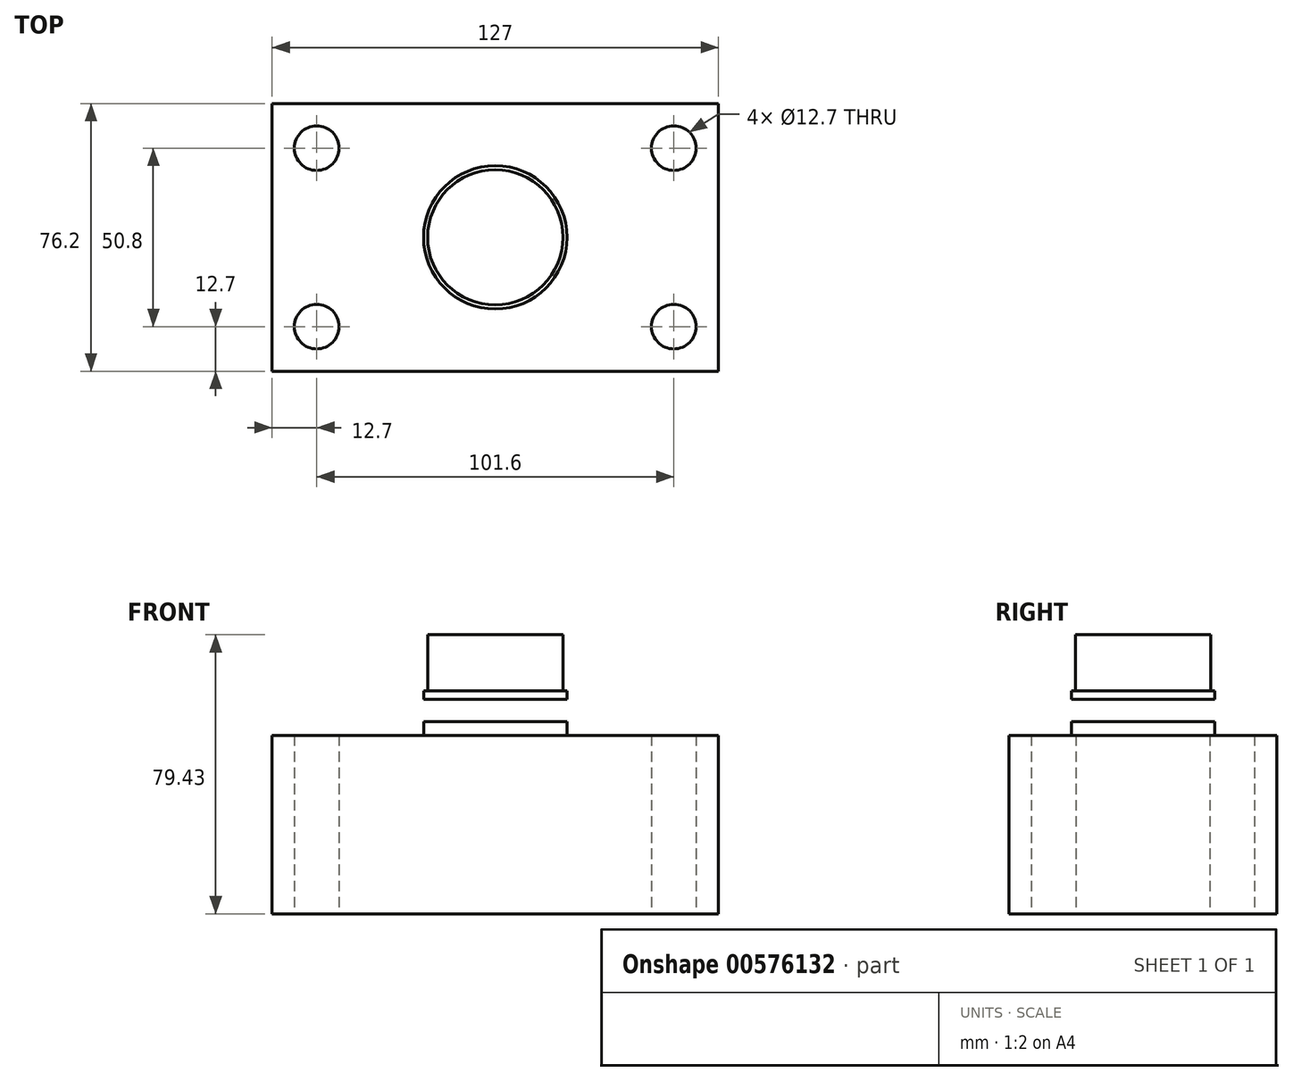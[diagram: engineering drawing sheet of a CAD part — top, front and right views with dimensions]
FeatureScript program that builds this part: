
annotation { "Feature Type Name" : "Feature", "Feature Type Description" : "" }
export const myFeature = defineFeature(function(context is Context, id is Id, definition is map)
    precondition{}
    {
        {
            var Q0;
            Q0=qCreatedBy(makeId("Top.planeOp"),FACE);
            var sketch = newSketch(context, id + "F0", { "sketchPlane" : qUnion([Q0])});
            skLineSegment(sketch, "E0.bottom", {"start": v(-63.5, 38.1) * mm, "end": v(63.5, 38.1) * mm});
            skLineSegment(sketch, "E0.top", {"start": v(-63.5, -38.1) * mm, "end": v(63.5, -38.1) * mm});
            skLineSegment(sketch, "E0.left", {"start": v(-63.5, 38.1) * mm, "end": v(-63.5, -38.1) * mm});
            skLineSegment(sketch, "E0.right", {"start": v(63.5, 38.1) * mm, "end": v(63.5, -38.1) * mm});
            skPoint(sketch, "E0.middle", {"position": v(0, 0) * mm});
            skCircle(sketch, "E1", {"center": v(-50.8, 25.4) * mm, "radius": 6.35 * mm});
            skCircle(sketch, "E2", {"center": v(-50.8, -25.4) * mm, "radius": 6.35 * mm});
            skCircle(sketch, "E3", {"center": v(50.8, 25.4) * mm, "radius": 6.35 * mm});
            skCircle(sketch, "E4", {"center": v(50.8, -25.4) * mm, "radius": 6.35 * mm});
            skSolve(sketch);
        }
        {
            var Q0;
            Q0 = qSketchRegion(id + "F0", true);
            extrude(context, id + "F1", {"entities" : qUnion([Q0]), "depth" : 50.8 * mm, "offsetDistance" : 25.4 * mm});
        }
        {
            var Q0;
            Q0=qCreatedBy(makeId("Front.planeOp"),FACE);
            var sketch = newSketch(context, id + "F2", { "sketchPlane" : qUnion([Q0])});
            skLineSegment(sketch, "E5.bottom", {"start": v(0, 50.8) * mm, "end": v(20.4, 50.8) * mm});
            skLineSegment(sketch, "E5.top", {"start": v(0, 63.5) * mm, "end": v(20.4, 63.5) * mm});
            skLineSegment(sketch, "E5.left", {"start": v(0, 50.8) * mm, "end": v(0, 63.5) * mm});
            skLineSegment(sketch, "E5.right", {"start": v(20.4, 50.8) * mm, "end": v(20.4, 63.5) * mm});
            skSolve(sketch);
        }
        {
            var Q0;
            Q0=makeQuery(id+"F2.imprint","IMPRINT",FACE,{"disambiguationData":[TD([[makeQuery(id+"F2.imprint","IMPRINT",EDGE,{"derivedFrom":sQuery(id+"F2.wireOp",EDGE,"E5.bottom")}),1.0]])]});
            var Q1;
            Q1=sQuery(id+"F2.wireOp",EDGE,"E5.left");
            revolve(context, id + "F3", {"operationType" : NewBodyOperationType.ADD, "entities" : qUnion([Q0]), "axis" : qUnion([Q1]), "revolveType" : RevolveType.FULL});
        }
        {
            var Q0;
            Q0=qCreatedBy(makeId("Front.planeOp"),FACE);
            var sketch = newSketch(context, id + "F4", { "sketchPlane" : qUnion([Q0])});
            skLineSegment(sketch, "E6.bottom", {"start": v(0, 63.5) * mm, "end": v(19.24, 63.5) * mm});
            skLineSegment(sketch, "E6.top", {"start": v(0, 79.43) * mm, "end": v(19.24, 79.43) * mm});
            skLineSegment(sketch, "E6.left", {"start": v(0, 63.5) * mm, "end": v(0, 79.43) * mm});
            skLineSegment(sketch, "E6.right", {"start": v(19.24, 63.5) * mm, "end": v(19.24, 79.43) * mm});
            skSolve(sketch);
        }
        {
            var Q0;
            Q0=makeQuery(id+"F4.imprint","IMPRINT",FACE,{"disambiguationData":[TD([[makeQuery(id+"F4.imprint","IMPRINT",EDGE,{"derivedFrom":sQuery(id+"F4.wireOp",EDGE,"E6.bottom")}),1.0]])]});
            var Q1;
            Q1=sQuery(id+"F4.wireOp",EDGE,"E6.left");
            revolve(context, id + "F5", {"operationType" : NewBodyOperationType.ADD, "entities" : qUnion([Q0]), "axis" : qUnion([Q1]), "revolveType" : RevolveType.FULL});
        }
        {
            var Q0;
            Q0=qCreatedBy(makeId("Front.planeOp"),FACE);
            var sketch = newSketch(context, id + "F6", { "sketchPlane" : qUnion([Q0])});
            skLineSegment(sketch, "E7.bottom", {"start": v(0, 54.68) * mm, "end": v(38.1, 54.68) * mm});
            skLineSegment(sketch, "E7.top", {"start": v(0, 61.03) * mm, "end": v(38.1, 61.03) * mm});
            skLineSegment(sketch, "E7.left", {"start": v(0, 54.68) * mm, "end": v(0, 61.03) * mm});
            skLineSegment(sketch, "E7.right", {"start": v(38.1, 54.68) * mm, "end": v(38.1, 61.03) * mm});
            skSolve(sketch);
        }
        {
            var Q0;
            Q0 = qSketchRegion(id + "F6", true);
            var Q1;
            Q1=sQuery(id+"F6.wireOp",EDGE,"E7.left");
            revolve(context, id + "F7", {"operationType" : NewBodyOperationType.REMOVE, "entities" : qUnion([Q0]), "axis" : qUnion([Q1]), "revolveType" : RevolveType.FULL, "oppositeDirection" : true});
        }
    });
